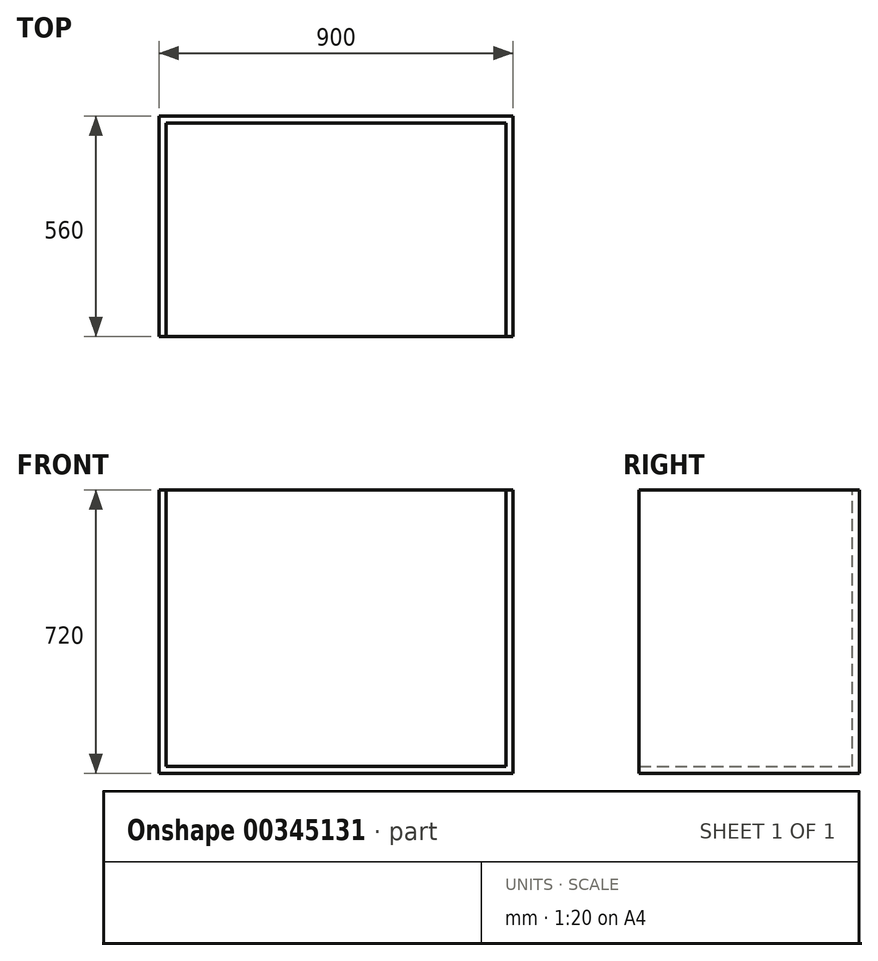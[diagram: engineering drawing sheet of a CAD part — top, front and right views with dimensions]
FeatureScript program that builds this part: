
annotation { "Feature Type Name" : "Feature", "Feature Type Description" : "" }
export const myFeature = defineFeature(function(context is Context, id is Id, definition is map)
    precondition{}
    {
        {
            var Q0;
            Q0=qCreatedBy(makeId("Front.planeOp"),FACE);
            var sketch = newSketch(context, id + "F0", { "sketchPlane" : qUnion([Q0])});
            skLineSegment(sketch, "E0.bottom", {"start": v(0, 0) * mm, "end": v(51.52, 0) * mm});
            skLineSegment(sketch, "E0.top", {"start": v(0, 46.93) * mm, "end": v(51.52, 46.93) * mm});
            skLineSegment(sketch, "E0.left", {"start": v(0, 0) * mm, "end": v(0, 46.93) * mm});
            skLineSegment(sketch, "E0.right", {"start": v(51.52, 0) * mm, "end": v(51.52, 46.93) * mm});
            skSolve(sketch);
        }
        {
            var Q0;
            Q0=makeQuery(id+"F0.imprint","IMPRINT",FACE,{"disambiguationData":[TD([[makeQuery(id+"F0.imprint","IMPRINT",EDGE,{"derivedFrom":sQuery(id+"F0.wireOp",EDGE,"E0.bottom")}),1.0]])]});
            extrude(context, id + "F1", {"entities" : qUnion([Q0]), "depth" : 560 * mm});
        }
        {
            var Q0;
            Q0=makeQuery(id+"F1.opExtrude","SWEPT_FACE",FACE,{"disambiguationData":[OSD([sQuery(id+"F0.wireOp",EDGE,"E0.left")])]});
            extrude(context, id + "F2", {"entities" : qUnion([Q0]), "operationType" : NewBodyOperationType.ADD, "oppositeDirection" : true, "depth" : 900 * mm});
        }
        {
            var Q0;
            {var subQ0=sQuery(id+"F0.wireOp",EDGE,"E0.bottom");Q0=makeQuery(id+"F2.boolean.opBoolean","MERGE",FACE,{"derivedFrom":[makeQuery(id+"F1.opExtrude","SWEPT_FACE",FACE,{"disambiguationData":[OSD([subQ0])]}),makeQuery(id+"F2.opExtrude","SWEPT_FACE",FACE,{"disambiguationData":[OSD([subQ0,sQuery(id+"F0.wireOp",EDGE,"E0.left")])]})]});}
            extrude(context, id + "F3", {"entities" : qUnion([Q0]), "operationType" : NewBodyOperationType.ADD, "oppositeDirection" : true, "depth" : 720 * mm});
        }
        {
            var Q0;
            {var subQ0=sQuery(id+"F0.wireOp",EDGE,"E0.left");var subQ1=sQuery(id+"F0.wireOp",EDGE,"E0.bottom");Q0=makeQuery(id+"F3.boolean.opBoolean","MERGE",FACE,{"derivedFrom":[makeQuery(id+"F2.boolean.opBoolean","MERGE",FACE,{"derivedFrom":[makeQuery(id+"F1.opExtrude","CAP_FACE",FACE,{"disambiguationData":[OSD([subQ1,sQuery(id+"F0.wireOp",EDGE,"E0.top"),subQ0,sQuery(id+"F0.wireOp",EDGE,"E0.right")])],"isStart":false}),makeQuery(id+"F2.opExtrude","SWEPT_FACE",FACE,{"disambiguationData":[OSD([subQ0]),TDD([makeQuery(id+"F1.opExtrude","CAP_EDGE",EDGE,{"disambiguationData":[OSD([subQ0])],"isStart":false})])]})]}),makeQuery(id+"F3.opExtrude","SWEPT_FACE",FACE,{"disambiguationData":[OSD([subQ1,subQ0]),TDD([makeQuery(id+"F2.boolean.opBoolean","MERGE",EDGE,{"derivedFrom":[makeQuery(id+"F1.opExtrude","CAP_EDGE",EDGE,{"disambiguationData":[OSD([subQ1])],"isStart":false}),makeQuery(id+"F2.opExtrude","SWEPT_EDGE",EDGE,{"disambiguationData":[OSD([subQ1,subQ0]),TDD([makeQuery(id+"F1.opExtrude","CAP_VERTEX",VERTEX,{"disambiguationData":[OSD([subQ1,subQ0])],"isStart":false})])]})]})])]})]});}
            var Q1;
            Q1=makeQuery(id+"F3.opExtrude","CAP_FACE",FACE,{"disambiguationData":[OSD([sQuery(id+"F0.wireOp",EDGE,"E0.bottom"),sQuery(id+"F0.wireOp",EDGE,"E0.left")])],"isStart":false});
            shell(context, id + "F4", {"entities" : qUnion([Q0, Q1]), "thickness" : 18 * mm});
        }
    });
